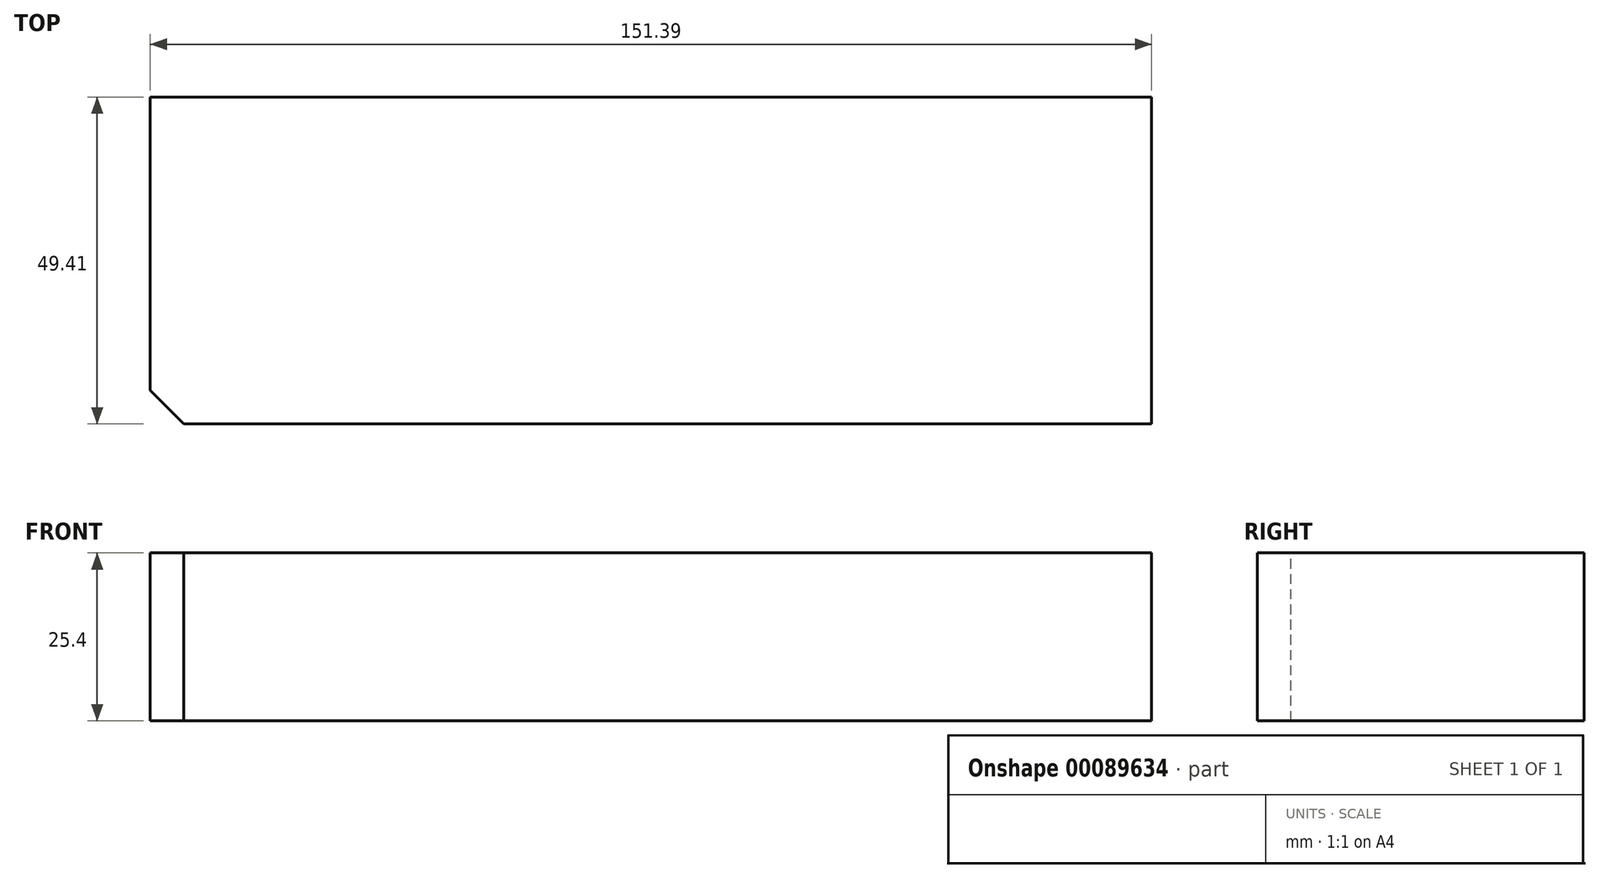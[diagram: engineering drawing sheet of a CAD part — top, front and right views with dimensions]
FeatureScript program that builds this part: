
annotation { "Feature Type Name" : "Feature", "Feature Type Description" : "" }
export const myFeature = defineFeature(function(context is Context, id is Id, definition is map)
    precondition{}
    {
        {
            var Q0;
            Q0=qCreatedBy(makeId("Top.planeOp"),FACE);
            var sketch = newSketch(context, id + "F0", { "sketchPlane" : qUnion([Q0])});
            skLineSegment(sketch, "E0.bottom", {"start": v(-72.35, 0) * mm, "end": v(79.04, 0) * mm});
            skLineSegment(sketch, "E0.top", {"start": v(-72.35, -49.41) * mm, "end": v(79.04, -49.41) * mm});
            skLineSegment(sketch, "E0.left", {"start": v(-72.35, 0) * mm, "end": v(-72.35, -49.41) * mm});
            skLineSegment(sketch, "E0.right", {"start": v(79.04, 0) * mm, "end": v(79.04, -49.41) * mm});
            skSolve(sketch);
        }
        {
            var Q0;
            Q0 = qSketchRegion(id + "F0", true);
            extrude(context, id + "F1", {"entities" : qUnion([Q0]), "depth" : 25.4 * mm});
        }
        {
            var Q0;
            Q0=makeQuery(id+"F1.opExtrude","SWEPT_EDGE",EDGE,{"disambiguationData":[OSD([sQuery(id+"F0.wireOp",EDGE,"E0.top"),sQuery(id+"F0.wireOp",EDGE,"E0.left")])]});
            chamfer(context, id + "F2", {"entities" : qUnion([Q0]), "width" : 5.08 * mm, "tangentPropagation" : true});
        }
    });
